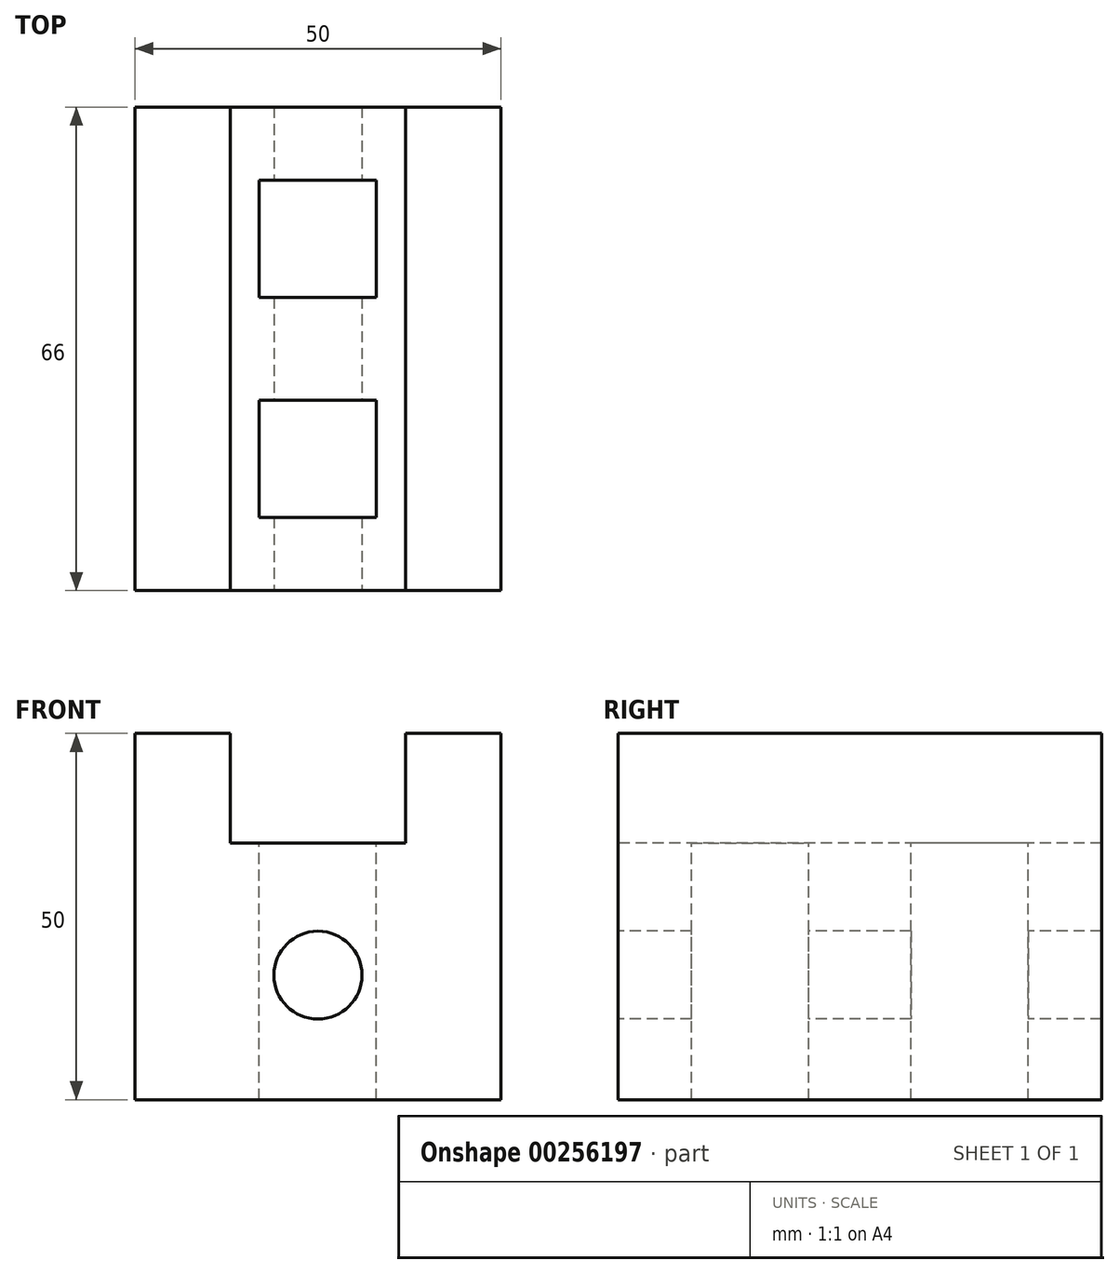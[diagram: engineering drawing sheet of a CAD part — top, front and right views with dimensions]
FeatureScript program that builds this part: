
annotation { "Feature Type Name" : "Feature", "Feature Type Description" : "" }
export const myFeature = defineFeature(function(context is Context, id is Id, definition is map)
    precondition{}
    {
        {
            var Q0;
            Q0=qCreatedBy(makeId("Top.planeOp"),FACE);
            var sketch = newSketch(context, id + "F0", { "sketchPlane" : qUnion([Q0])});
            skLineSegment(sketch, "E0.bottom", {"start": v(0, 0) * mm, "end": v(50, 0) * mm});
            skLineSegment(sketch, "E0.top", {"start": v(0, 66) * mm, "end": v(50, 66) * mm});
            skLineSegment(sketch, "E0.left", {"start": v(0, 0) * mm, "end": v(0, 66) * mm});
            skLineSegment(sketch, "E0.right", {"start": v(50, 0) * mm, "end": v(50, 66) * mm});
            skSolve(sketch);
        }
        {
            var Q0;
            Q0=makeQuery(id+"F0.imprint","IMPRINT",FACE,{"disambiguationData":[TD([[makeQuery(id+"F0.imprint","IMPRINT",EDGE,{"derivedFrom":sQuery(id+"F0.wireOp",EDGE,"E0.bottom")}),1.0]])]});
            extrude(context, id + "F1", {"entities" : qUnion([Q0]), "depth" : 50 * mm});
        }
        {
            var Q0;
            Q0=makeQuery(id+"F1.opExtrude","SWEPT_FACE",FACE,{"disambiguationData":[OSD([sQuery(id+"F0.wireOp",EDGE,"E0.bottom")])]});
            var sketch = newSketch(context, id + "F2", { "sketchPlane" : qUnion([Q0])});
            skLineSegment(sketch, "E1.bottom", {"start": v(13, 50) * mm, "end": v(37, 50) * mm});
            skLineSegment(sketch, "E1.top", {"start": v(13, 35) * mm, "end": v(37, 35) * mm});
            skLineSegment(sketch, "E1.left", {"start": v(13, 50) * mm, "end": v(13, 35) * mm});
            skLineSegment(sketch, "E1.right", {"start": v(37, 50) * mm, "end": v(37, 35) * mm});
            skSolve(sketch);
        }
        {
            var Q0;
            Q0=makeQuery(id+"F2.imprint","IMPRINT",FACE,{"disambiguationData":[TD([[makeQuery(id+"F2.imprint","IMPRINT",EDGE,{"derivedFrom":sQuery(id+"F2.wireOp",EDGE,"E1.bottom")}),-1.0]])]});
            extrude(context, id + "F3", {"entities" : qUnion([Q0]), "operationType" : NewBodyOperationType.REMOVE, "oppositeDirection" : true, "depth" : 66 * mm});
        }
        {
            var Q0;
            Q0=makeQuery(id+"F1.opExtrude","SWEPT_FACE",FACE,{"disambiguationData":[OSD([sQuery(id+"F0.wireOp",EDGE,"E0.bottom")])]});
            var sketch = newSketch(context, id + "F4", { "sketchPlane" : qUnion([Q0])});
            skCircle(sketch, "E2", {"center": v(25, 17) * mm, "radius": 6 * mm});
            skSolve(sketch);
        }
        {
            var Q0;
            Q0=makeQuery(id+"F4.imprint","IMPRINT",FACE,{"disambiguationData":[TD([[makeQuery(id+"F4.imprint","IMPRINT",EDGE,{"derivedFrom":sQuery(id+"F4.wireOp",EDGE,"E2")}),1.0]])]});
            extrude(context, id + "F5", {"entities" : qUnion([Q0]), "operationType" : NewBodyOperationType.REMOVE, "oppositeDirection" : true, "depth" : 66 * mm});
        }
        {
            var Q0;
            Q0=makeQuery(id+"F3.boolean.opBoolean","COPY",FACE,{"derivedFrom":makeQuery(id+"F3.opExtrude","SWEPT_FACE",FACE,{"disambiguationData":[OSD([sQuery(id+"F2.wireOp",EDGE,"E1.top")])]})});
            var sketch = newSketch(context, id + "F6", { "sketchPlane" : qUnion([Q0])});
            skLineSegment(sketch, "E3.bottom", {"start": v(19, 10) * mm, "end": v(31, 10) * mm});
            skLineSegment(sketch, "E3.top", {"start": v(19, 26) * mm, "end": v(31, 26) * mm});
            skLineSegment(sketch, "E3.left", {"start": v(19, 10) * mm, "end": v(19, 26) * mm});
            skLineSegment(sketch, "E3.right", {"start": v(31, 10) * mm, "end": v(31, 26) * mm});
            skLineSegment(sketch, "E4.bottom", {"start": v(31, 26) * mm, "end": v(19, 26) * mm});
            skLineSegment(sketch, "E4.top", {"start": v(31, 40) * mm, "end": v(19, 40) * mm});
            skLineSegment(sketch, "E5.top", {"start": v(31, 56) * mm, "end": v(19, 56) * mm});
            skLineSegment(sketch, "E5.left", {"start": v(31, 40) * mm, "end": v(31, 56) * mm});
            skLineSegment(sketch, "E5.right", {"start": v(19, 40) * mm, "end": v(19, 56) * mm});
            skSolve(sketch);
        }
        {
            var Q0;
            Q0=makeQuery(id+"F6.imprint","IMPRINT",FACE,{"disambiguationData":[TD([[makeQuery(id+"F6.imprint","IMPRINT",EDGE,{"derivedFrom":sQuery(id+"F6.wireOp",EDGE,"E4.top")}),-1.0]])]});
            var Q1;
            Q1=makeQuery(id+"F6.imprint","IMPRINT",FACE,{"disambiguationData":[TD([[makeQuery(id+"F6.imprint","IMPRINT",EDGE,{"derivedFrom":sQuery(id+"F6.wireOp",EDGE,"E3.bottom")}),1.0]])]});
            extrude(context, id + "F7", {"entities" : qUnion([Q0, Q1]), "operationType" : NewBodyOperationType.REMOVE, "oppositeDirection" : true, "depth" : 35 * mm});
        }
        {
            var Q0;
            Q0=makeQuery(id+"F3.boolean.opBoolean","COPY",FACE,{"derivedFrom":makeQuery(id+"F3.opExtrude","SWEPT_FACE",FACE,{"disambiguationData":[OSD([sQuery(id+"F2.wireOp",EDGE,"E1.top")])]})});
            var sketch = newSketch(context, id + "F8", { "sketchPlane" : qUnion([Q0])});
            skLineSegment(sketch, "E6", {"start": v(31, 10) * mm, "end": v(17, 10) * mm});
            skPoint(sketch, "E6.endSnap0", {"position": v(25, 10) * mm});
            skLineSegment(sketch, "E7", {"start": v(17, 10) * mm, "end": v(31, 10) * mm});
            skLineSegment(sketch, "E8.bottom", {"start": v(17, 10) * mm, "end": v(33, 10) * mm});
            skLineSegment(sketch, "E8.top", {"start": v(17, 26) * mm, "end": v(33, 26) * mm});
            skLineSegment(sketch, "E8.left", {"start": v(17, 10) * mm, "end": v(17, 26) * mm});
            skLineSegment(sketch, "E8.right", {"start": v(33, 10) * mm, "end": v(33, 26) * mm});
            skLineSegment(sketch, "E9.bottom", {"start": v(19, 40) * mm, "end": v(17, 40) * mm});
            skLineSegment(sketch, "E9.top", {"start": v(19, 56) * mm, "end": v(17, 56) * mm});
            skLineSegment(sketch, "E9.left", {"start": v(19, 40) * mm, "end": v(19, 56) * mm});
            skLineSegment(sketch, "E9.right", {"start": v(17, 40) * mm, "end": v(17, 56) * mm});
            skLineSegment(sketch, "E10.bottom", {"start": v(17, 56) * mm, "end": v(33, 56) * mm});
            skLineSegment(sketch, "E10.top", {"start": v(17, 40) * mm, "end": v(33, 40) * mm});
            skLineSegment(sketch, "E10.left", {"start": v(17, 56) * mm, "end": v(17, 40) * mm});
            skLineSegment(sketch, "E10.right", {"start": v(33, 56) * mm, "end": v(33, 40) * mm});
            skSolve(sketch);
        }
        {
            var Q0;
            {var subQ0=sQuery(id+"F8.wireOp",EDGE,"E9.left");Q0=makeQuery(id+"F8.imprint","IMPRINT",FACE,{"disambiguationData":[TD([[makeQuery(id+"F8.imprint","IMPRINT",EDGE,{"derivedFrom":subQ0}),1.0]])]});}
            var Q1;
            {var subQ2=sQuery(id+"F8.wireOp",EDGE,"E10.right");Q1=makeQuery(id+"F8.imprint","IMPRINT",FACE,{"disambiguationData":[TD([[makeQuery(id+"F8.imprint","IMPRINT",EDGE,{"derivedFrom":subQ2}),-1.0]])]});}
            var Q2;
            {var subQ2=sQuery(id+"F8.wireOp",EDGE,"E8.left");Q2=makeQuery(id+"F8.imprint","IMPRINT",FACE,{"disambiguationData":[TD([[makeQuery(id+"F8.imprint","IMPRINT",EDGE,{"derivedFrom":subQ2}),-1.0]])]});}
            var Q3;
            {var subQ2=sQuery(id+"F8.wireOp",EDGE,"E8.right");Q3=makeQuery(id+"F8.imprint","IMPRINT",FACE,{"disambiguationData":[TD([[makeQuery(id+"F8.imprint","IMPRINT",EDGE,{"derivedFrom":subQ2}),1.0]])]});}
            extrude(context, id + "F9", {"entities" : qUnion([Q0, Q1, Q2, Q3]), "operationType" : NewBodyOperationType.REMOVE, "oppositeDirection" : true, "depth" : 35 * mm});
        }
    });
